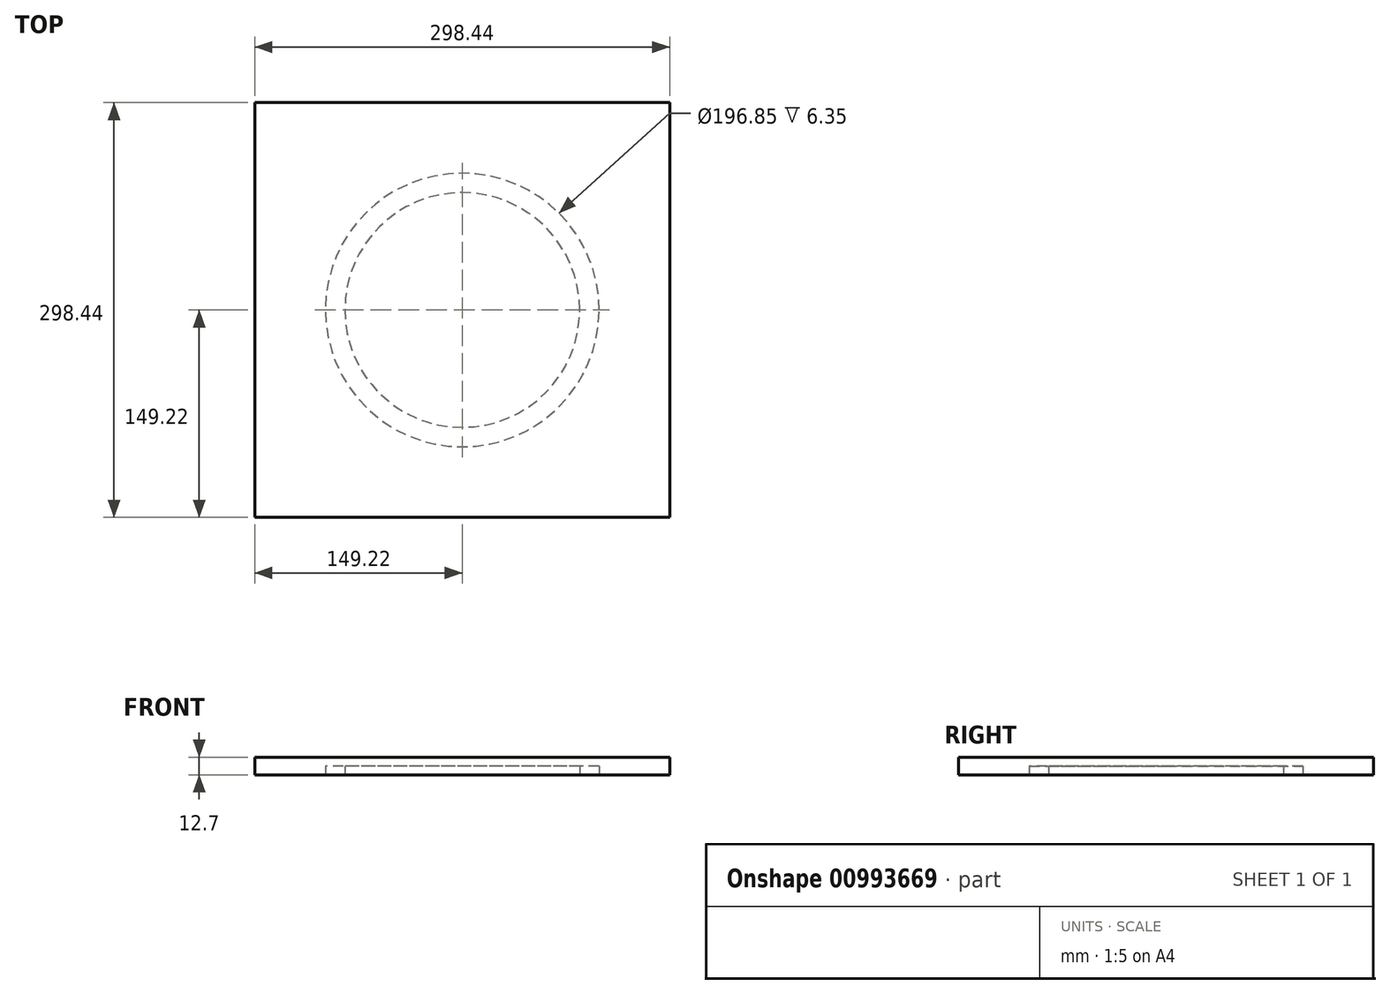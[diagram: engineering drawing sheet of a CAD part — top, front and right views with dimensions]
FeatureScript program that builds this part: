
annotation { "Feature Type Name" : "Feature", "Feature Type Description" : "" }
export const myFeature = defineFeature(function(context is Context, id is Id, definition is map)
    precondition{}
    {
        {
            var Q0;
            Q0=qCreatedBy(makeId("Top.planeOp"),FACE);
            var sketch = newSketch(context, id + "F0", { "sketchPlane" : qUnion([Q0])});
            skLineSegment(sketch, "E0.bottom", {"start": v(-149.22, 149.23) * mm, "end": v(149.23, 149.23) * mm});
            skLineSegment(sketch, "E0.top", {"start": v(-149.23, -149.23) * mm, "end": v(149.22, -149.23) * mm});
            skLineSegment(sketch, "E0.left", {"start": v(-149.22, 149.23) * mm, "end": v(-149.23, -149.23) * mm});
            skLineSegment(sketch, "E0.right", {"start": v(149.23, 149.23) * mm, "end": v(149.22, -149.23) * mm});
            skPoint(sketch, "E0.middle", {"position": v(0, 0) * mm});
            skCircle(sketch, "E1", {"center": v(0, 0) * mm, "radius": 84.46 * mm});
            skCircle(sketch, "E2", {"center": v(0, 0) * mm, "radius": 98.43 * mm});
            skSolve(sketch);
        }
        {
            var Q0;
            Q0=makeQuery(id+"F0.imprint","IMPRINT",FACE,{"disambiguationData":[TD([[makeQuery(id+"F0.imprint","IMPRINT",EDGE,{"derivedFrom":sQuery(id+"F0.wireOp",EDGE,"E1")}),1.0]])]});
            var Q1;
            Q1=makeQuery(id+"F0.imprint","IMPRINT",FACE,{"disambiguationData":[TD([[makeQuery(id+"F0.imprint","IMPRINT",EDGE,{"derivedFrom":sQuery(id+"F0.wireOp",EDGE,"E1")}),-1.0]])]});
            var Q2;
            Q2=makeQuery(id+"F0.imprint","IMPRINT",FACE,{"disambiguationData":[TD([[makeQuery(id+"F0.imprint","IMPRINT",EDGE,{"derivedFrom":sQuery(id+"F0.wireOp",EDGE,"E0.bottom")}),-1.0]])]});
            extrude(context, id + "F1", {"entities" : qUnion([Q0, Q1, Q2]), "depth" : 12.7 * mm, "offsetDistance" : 25.4 * mm});
        }
        {
            var Q0;
            Q0=makeQuery(id+"F0.imprint","IMPRINT",FACE,{"disambiguationData":[TD([[makeQuery(id+"F0.imprint","IMPRINT",EDGE,{"derivedFrom":sQuery(id+"F0.wireOp",EDGE,"E1")}),-1.0]])]});
            var Q1;
            Q1=sQuery(id+"F0.wireOp",EDGE,"E2");
            extrude(context, id + "F2", {"entities" : qUnion([Q0]), "operationType" : NewBodyOperationType.REMOVE, "surfaceEntities" : qUnion([Q1]), "depth" : 6.35 * mm, "offsetDistance" : 25.4 * mm});
        }
    });
